# Revit family: Mixing_Valve-Thermostatic-Leonard_Valve-Point_Of_Use-LF_Series
name_source: partatom
category: Pipe Accessories
revit_build: Autodesk Revit 2015 (Build: 20140905_0730(x64)
units: mm (PartAtom-declared; Revit-internal decimal feet)

## types (3) — shared parameters
Date Modified = April 28, 2015
Description = See Part Description
Equipment Abbreviation = MV
Family Version = 1.0
Manufacturer = Leonard Valve Company
Model = See Part Number
Model Disclaimer = For More Information, Contact Leonard Valve Company
Product Documentation Link = http://leonardvalve.industrysuite.com
Product Page URL = http://www.leonardvalve.com
Product data url = https://bimobject.com
URL = http://www.leonardvalve.com

## per-type parameters (varying)
| type | z Bottom Piece Radius | z Middle to Bottom | z Middle to Bottom Pipe | z Outside Pipe Radius | z Part Pipe Radius Inside | z Part Pipe Radius Outside | z Pipe Radius | z Type Size | z Width Middle |
| 170 | 0.5175 " | 2.149 " | 0.805 " | 0.416 " | 0.25 " | 0.3325 " | 0.1875 " | 1 | 2.273 " |
| 270 | 0.55 " | 1.9 " | 0.56 " | 0.45 " | 0.34 " | 0.375 " | 0.25 " | 2 | 3.8 " |
| 370 | 0.57 " | 1.9 " | 0.81 " | 0.53 " | 0.465 " | 0.5 " | 0.375 " | 3 | 2.88 " |

## geometry (parser evidence)
native form markers: Blend x12, Sweep x2
no freeform markers — native parametric forms only
